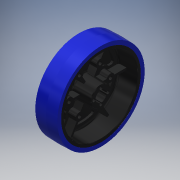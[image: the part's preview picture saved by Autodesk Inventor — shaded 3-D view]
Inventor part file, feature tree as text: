
AUTODESK INVENTOR PART (.ipt)
format: ipt  version: 2017 (Build 210142000, 142)  size: 1,393,152 bytes
history: native  units: in
note: dims shown in document units (in); Inventor stores cm internally (conversion verified against a paired STEP export)
features: other x2, extrude x1, sketch x1
ambient origin geometry x8: Origin, YZ Plane, XZ Plane, XY Plane, X Axis, Y Axis, Z Axis, Center Point
bodies: Solid1 (feature_tree), Solid2 (feature_tree)
feature tree (4):
  extrude  "Extrusion1"  Depth=1.0in TaperAngle=0.0deg
  sketch  "Sketch1"  dims[d0=0.5in d1=1.0in d2=0.0in]
  other  "4in Wheel Intergreated Hub 8mm Rev2_1:1"
  other  "4in Tread_2:1"
